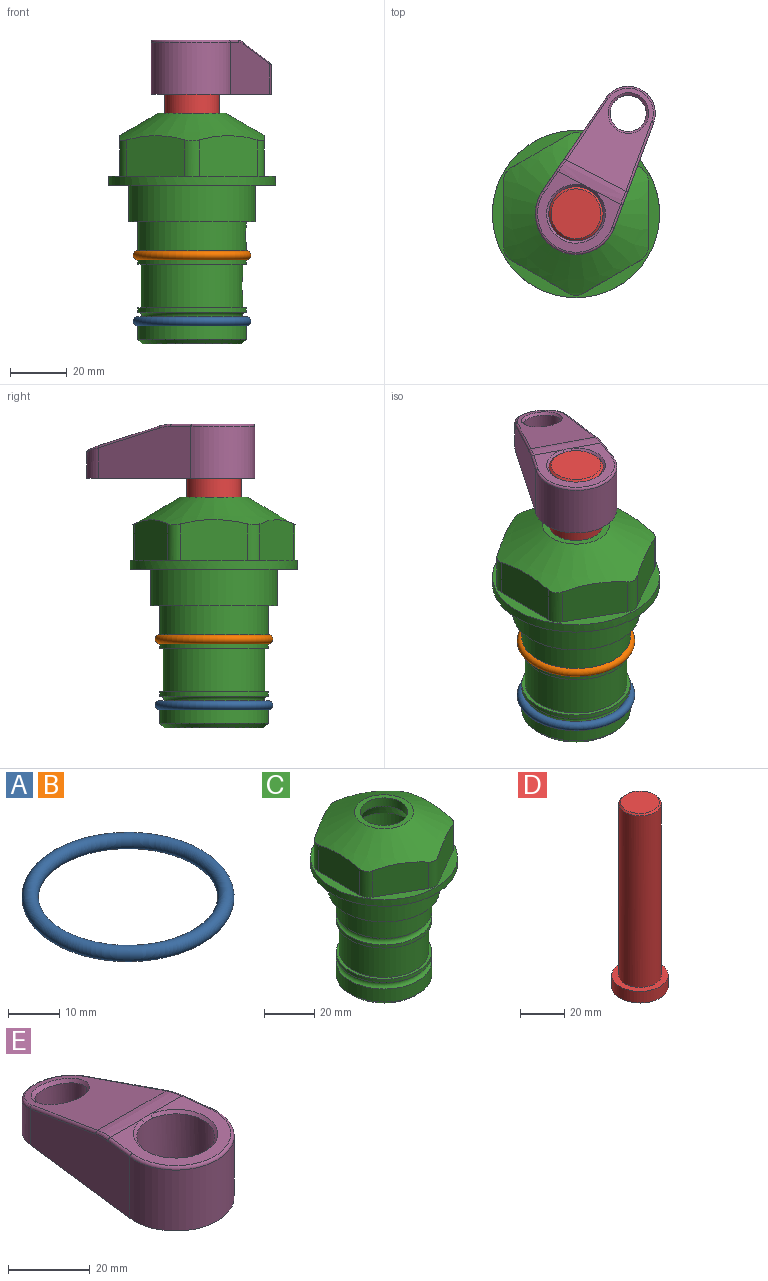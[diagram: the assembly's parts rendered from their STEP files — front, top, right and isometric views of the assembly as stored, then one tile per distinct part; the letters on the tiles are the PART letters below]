
ASSEMBLY  parts=5 mates=4
PART A: 1 faces, bbox 44.7x44.7x3.2 mm
  f0: torus R=19.05mm, axis (0,0,1), area 1193.9mm2
PART B: same geometry as A
PART C: 36 faces, bbox 58.7x58.7x81 mm
  f0: cylinder r=17.78mm len=35.56mm, axis (0,0,1), area 1670.8mm2, adj f23,f24,f31
  f1: cylinder r=19.05mm len=38.1mm, axis (0,0,1), area 1191.9mm2, adj f26,f27,f30
  f2: plane 58.66x58.66mm, normal (0,0,-1), area 1150.6mm2, adj f3,f28
  f3: cylinder r=29.33mm len=58.66mm, axis (0,0,-1), area 585.1mm2, adj f2,f4
  f4: plane 58.66x58.66mm, normal (0,0,1), area 475.9mm2, adj f3,f5,f6,f7,f8,f9,f10,f11
  f5: plane 20.32x14.34mm, normal (-0.5,0.87,0), area 324.4mm2, adj f4,f15,f16,f17
  f6: plane 20.32x14.34mm, normal (0.5,0.87,0), area 324.4mm2, adj f4,f14,f15,f17
  f7: plane 23.48x14.34mm, normal (1,0,0), area 324.4mm2, adj f4,f13,f14,f17
  f8: plane 20.32x14.34mm, normal (0.5,-0.87,0), area 324.4mm2, adj f4,f12,f13,f17
  f9: plane 20.32x14.34mm, normal (-0.5,-0.87,0), area 324.4mm2, adj f4,f11,f12,f17
  f10: plane 23.48x14.34mm, normal (-1,0,0), area 324.4mm2, adj f4,f11,f16,f17
  f11: cylinder r=5.08mm len=12.85mm, axis (0,0,-1), area 67.2mm2, adj f4,f9,f10,f17
  f12: cylinder r=5.08mm len=12.85mm, axis (0,0,-1), area 67.2mm2, adj f4,f8,f9,f17
  f13: cylinder r=5.08mm len=12.85mm, axis (0,0,-1), area 67.2mm2, adj f4,f7,f8,f17
  f14: cylinder r=5.08mm len=12.85mm, axis (0,0,-1), area 67.2mm2, adj f4,f6,f7,f17
  f15: cylinder r=5.08mm len=12.85mm, axis (0,0,-1), area 67.2mm2, adj f4,f5,f6,f17
  f16: cylinder r=5.08mm len=12.85mm, axis (0,0,-1), area 67.2mm2, adj f4,f5,f10,f17
  f17: cone r=11.73mm half-angle=60deg, axis (0,0,-1), area 2071.8mm2, adj f5,f6,f7,f8,f9,f10,f11,f12
  f18: plane 23.46x23.46mm, normal (0,0,1), area 147.4mm2, adj f17,f35
  f19: plane 34.93x34.93mm, normal (0,0,-1), area 958mm2, adj f29
  f20: cylinder r=19.05mm len=38.1mm, axis (0,0,1), area 760.1mm2, adj f21,f29
  f21: torus R=19.05mm, axis (0,0,1), area 565.3mm2, adj f20,f22
  f22: cylinder r=19.05mm len=38.1mm, axis (0,0,1), area 190mm2, adj f21,f23
  f23: plane 38.1x38.1mm, normal (0,0,1), area 146.9mm2, adj f0,f22
  f24: plane 38.1x38.1mm, normal (0,0,-1), area 146.9mm2, adj f0,f25
  f25: cylinder r=19.05mm len=38.1mm, axis (0,0,1), area 190mm2, adj f24,f26
  f26: torus R=19.05mm, axis (0,0,1), area 565.3mm2, adj f1,f25
  f27: plane 44.45x44.45mm, normal (0,0,-1), area 411.7mm2, adj f1,f28
  f28: cylinder r=22.23mm len=44.45mm, axis (0,0,1), area 1773.5mm2, adj f2,f27
  f29: cone r=19.05mm half-angle=45deg, axis (0,0,1), area 257.5mm2, adj f19,f20
  f30: cylinder r=3.17mm len=6.75mm, axis (-1,0,0), area 128mm2, adj f1,f33
  f31: cylinder r=3.17mm len=6.35mm, axis (-1,0,0), area 102.5mm2, adj f0,f33
  f32: plane 25.4x25.4mm, normal (0,0,1), area 506.7mm2, adj f33
  f33: cylinder r=12.7mm len=66.42mm, axis (0,0,-1), area 5236.2mm2, adj f30,f31,f32,f34
  f34: cone r=9.53mm half-angle=30deg, axis (0,0,-1), area 443.4mm2, adj f33,f35
  f35: cylinder r=9.53mm len=19.05mm, axis (0,0,-1), area 240.9mm2, adj f18,f34
PART D: 6 faces, bbox 25.4x25.4x101.6 mm
  f0: plane 17.46x17.46mm, normal (0,0,1), area 239.5mm2, adj f5
  f1: plane 25.4x25.4mm, normal (0,0,-1), area 506.7mm2, adj f2
  f2: cylinder r=12.7mm len=25.4mm, axis (0,0,1), area 506.7mm2, adj f1,f3
  f3: plane 25.4x25.4mm, normal (0,0,1), area 221.7mm2, adj f2,f4
  f4: cylinder r=9.53mm len=94.46mm, axis (0,0,1), area 5653mm2, adj f3,f5
  f5: cone r=8.73mm half-angle=45deg, axis (0,0,-1), area 64.4mm2, adj f0,f4
PART E: 31 faces, bbox 31.7x65.5x19.8 mm
  f0: plane 39.12x18.26mm, normal (0.99,0.12,0), area 612.2mm2, adj f1,f4,f7,f11,f13,f15
  f1: cylinder r=9.53mm len=18.91mm, axis (0,0,-1), area 296.1mm2, adj f0,f2,f7,f17
  f2: plane 39.12x18.26mm, normal (-0.99,0.12,0), area 612.2mm2, adj f1,f4,f7,f12,f14,f16
  f3: cylinder r=6.35mm len=12.7mm, axis (0,0,-1), area 362.4mm2, adj f7,f18
  f4: cylinder r=14.29mm len=28.58mm, axis (0,0,-1), area 882.2mm2, adj f0,f2,f7,f10
  f5: cylinder r=9.53mm len=19.05mm, axis (0,0,-1), area 1092.6mm2, adj f7,f19,f20
  f6: plane 26.99x23.69mm, normal (0,0,1), area 216.2mm2, adj f9,f10,f11,f12,f19
  f7: plane 63.5x28.58mm, normal (0,0,-1), area 661.8mm2, adj f0,f1,f2,f3,f4,f5,f22,f23
  f8: plane 33.52x23.6mm, normal (0,0.26,0.97), area 486mm2, adj f9,f15,f16,f17,f18
  f9: cylinder r=19.05mm len=24.72mm, axis (1,0,0), area 120.4mm2, adj f6,f8,f13,f14,f20
  f10: torus R=13.49mm, axis (0,0,1), area 59mm2, adj f4,f6,f11,f12
  f11: cylinder r=0.79mm len=8.67mm, axis (0.12,-0.99,0), area 10.8mm2, adj f0,f6,f10,f13
  f12: cylinder r=0.79mm len=8.67mm, axis (0.12,0.99,0), area 10.8mm2, adj f2,f6,f10,f14
  f13: bspline ~4.95x1.42mm, area 6.1mm2, adj f0,f9,f11,f15
  f14: bspline ~4.95x1.42mm, area 6.1mm2, adj f2,f9,f12,f16
  f15: cylinder r=0.79mm len=25.95mm, axis (0.12,-0.96,0.26), area 32.9mm2, adj f0,f8,f13,f17
  f16: cylinder r=0.79mm len=25.95mm, axis (0.12,0.96,-0.26), area 32.9mm2, adj f2,f8,f14,f17
  f17: bspline ~18.91x8.38mm, area 30mm2, adj f1,f8,f15,f16
  f18: bspline ~14.29x14.29mm, area 48.3mm2, adj f3,f8
  f19: cone r=9.53mm half-angle=45deg, axis (0,0,1), area 66.5mm2, adj f5,f6,f20
  f20: bspline ~3.22x0.96mm, area 3.5mm2, adj f5,f9,f19
  f21: plane 2.75x2.72mm, normal (0,0,-1), area 2.9mm2, adj f23,f25,f28
  f22: plane 23.05x15.88mm, normal (-0.99,-0.12,0), area 323.6mm2, adj f7,f25,f26,f27,f28,f29
  f23: plane 23.05x15.88mm, normal (0.99,-0.12,0), area 323.6mm2, adj f7,f21,f25,f27,f28,f30
  f24: cylinder r=9.53mm len=10.69mm, axis (0,0,-1), area 114.7mm2, adj f7,f27,f29,f30
  f25: cylinder r=12.7mm len=20.59mm, axis (0,0,-1), area 381.1mm2, adj f7,f21,f22,f23,f26,f28
  f26: plane 2.75x2.72mm, normal (0,0,-1), area 2.9mm2, adj f22,f25,f28
  f27: plane 19.72x18.37mm, normal (0,-0.26,-0.97), area 291.8mm2, adj f22,f23,f24,f28,f29,f30
  f28: cylinder r=15.88mm len=19.92mm, axis (1,0,0), area 54.8mm2, adj f21,f22,f23,f25,f26,f27
  f29: cylinder r=1.59mm len=11mm, axis (0,0,-1), area 34.7mm2, adj f7,f22,f24,f27
  f30: cylinder r=1.59mm len=11mm, axis (0,0,-1), area 34.7mm2, adj f7,f23,f24,f27
PLACE A t=(0,0,-23.18)mm
PLACE B at identity
PLACE C at identity fixed
PLACE D rot(axis=(0,0,-1),27.5deg) t=(0,0,-12.45)mm
PLACE E rot(axis=(0,0,-1),27.5deg) t=(0,0,-12.45)mm
MATE fastened A.f0 <-> C.f0  axis (0,0,1) through (0,0,-47.69)mm
MATE fastened E.f4 <-> D.f2  axis (0,0,1) through (0,0,51.05)mm
MATE fastened B.f0 <-> C.f0  axis (0,0,1) through (0,0,-24.51)mm
MATE cylindrical D.f2 <-> C.f0  axis (0,0,-1) through (0,0,-50.55)mm
